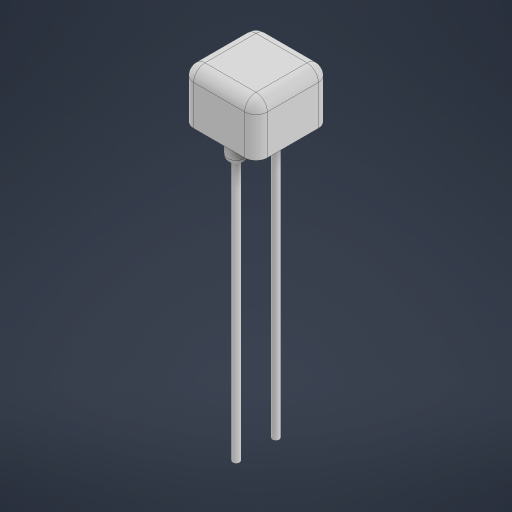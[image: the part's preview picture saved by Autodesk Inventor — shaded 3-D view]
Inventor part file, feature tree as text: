
AUTODESK INVENTOR PART (.ipt)
format: ipt  version: 2024 (Build 280153000, 153)  size: 223,232 bytes
history: native  units: in
note: dims shown in document units (in); Inventor stores cm internally (conversion verified against a paired STEP export)
features: extrude x3, sketch x3, fillet x2
ambient origin geometry x8: Origin, YZ Plane, XZ Plane, XY Plane, X Axis, Y Axis, Z Axis, Center Point
bodies: Solid1 (feature_tree)
feature tree (8):
  extrude  "Extrusion1"  Depth=0.2559in
  fillet  "Fillet1"  Radius=0.0394in
  extrude  "Extrusion2"  Depth=0.0591in
  extrude  "Extrusion3"  Depth=0.0394in
  fillet  "Fillet2"  Radius=0.0591in
  sketch  "Sketch1"  dims[d0=0.2559in d1=0.2559in d2=0.0394in]
  sketch  "Sketch2"  dims[d5=0.0591in d7=0.0591in]
  sketch  "Sketch3"  dims[d8=0.1772in d9=0.0in d10=0.0394in d13=0.0591in d14=0.0591in d15=0.0787in d16=0.0in d17=0.0236in d18=0.0236in d19=0.9055in d20=0.0in d21=0.0177in d11=0.0in d12=0.0in]
